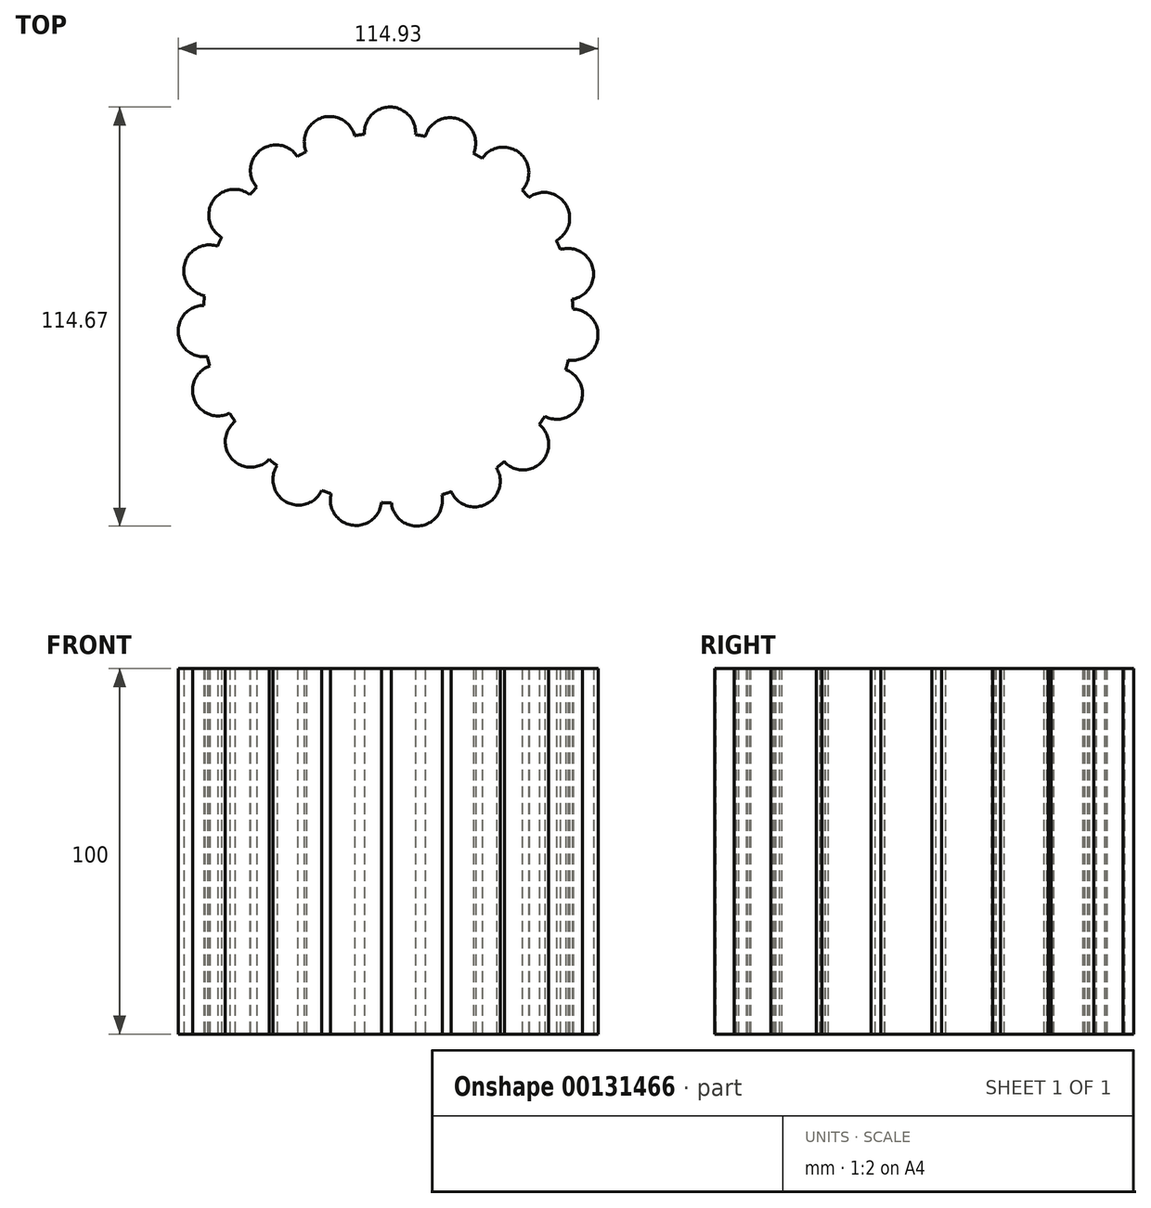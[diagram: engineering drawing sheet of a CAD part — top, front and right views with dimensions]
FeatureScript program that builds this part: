
annotation { "Feature Type Name" : "Feature", "Feature Type Description" : "" }
export const myFeature = defineFeature(function(context is Context, id is Id, definition is map)
    precondition{}
    {
        {
            var Q0;
            Q0=qCreatedBy(makeId("Top.planeOp"),FACE);
            var sketch = newSketch(context, id + "F0", { "sketchPlane" : qUnion([Q0])});
            skCircle(sketch, "E0", {"center": v(0, 0) * mm, "radius": 50.63 * mm});
            skCircle(sketch, "E1", {"center": v(-15.97, 48.05) * mm, "radius": 7 * mm});
            skCircle(sketch, "E2.1.0", {"center": v(-30.7, 40.26) * mm, "radius": 7 * mm});
            skCircle(sketch, "E2.2.0", {"center": v(-42.11, 28.11) * mm, "radius": 7 * mm});
            skCircle(sketch, "E2.3.0", {"center": v(-48.96, 12.92) * mm, "radius": 7 * mm});
            skCircle(sketch, "E2.4.0", {"center": v(-50.5, -3.68) * mm, "radius": 7 * mm});
            skCircle(sketch, "E2.5.0", {"center": v(-46.57, -19.88) * mm, "radius": 7 * mm});
            skCircle(sketch, "E2.6.0", {"center": v(-37.6, -33.92) * mm, "radius": 7 * mm});
            skCircle(sketch, "E2.7.0", {"center": v(-24.54, -44.3) * mm, "radius": 7 * mm});
            skCircle(sketch, "E2.8.0", {"center": v(-8.83, -49.86) * mm, "radius": 7 * mm});
            skCircle(sketch, "E2.9.0", {"center": v(7.84, -50.02) * mm, "radius": 7 * mm});
            skCircle(sketch, "E2.10.0", {"center": v(23.66, -44.77) * mm, "radius": 7 * mm});
            skCircle(sketch, "E2.11.0", {"center": v(36.91, -34.66) * mm, "radius": 7 * mm});
            skCircle(sketch, "E2.12.0", {"center": v(46.17, -20.8) * mm, "radius": 7 * mm});
            skCircle(sketch, "E2.13.0", {"center": v(50.42, -4.68) * mm, "radius": 7 * mm});
            skCircle(sketch, "E2.14.0", {"center": v(49.2, 11.94) * mm, "radius": 7 * mm});
            skCircle(sketch, "E2.15.0", {"center": v(42.66, 27.27) * mm, "radius": 7 * mm});
            skCircle(sketch, "E2.16.0", {"center": v(31.5, 39.65) * mm, "radius": 7 * mm});
            skCircle(sketch, "E2.17.0", {"center": v(16.91, 47.73) * mm, "radius": 7 * mm});
            skCircle(sketch, "E2.18.0", {"center": v(0.5, 50.63) * mm, "radius": 7 * mm});
            skSolve(sketch);
        }
        {
            var Q0;
            Q0 = qSketchRegion(id + "F0", true);
            extrude(context, id + "F1", {"entities" : qUnion([Q0]), "depth" : 100 * mm});
        }
    });
